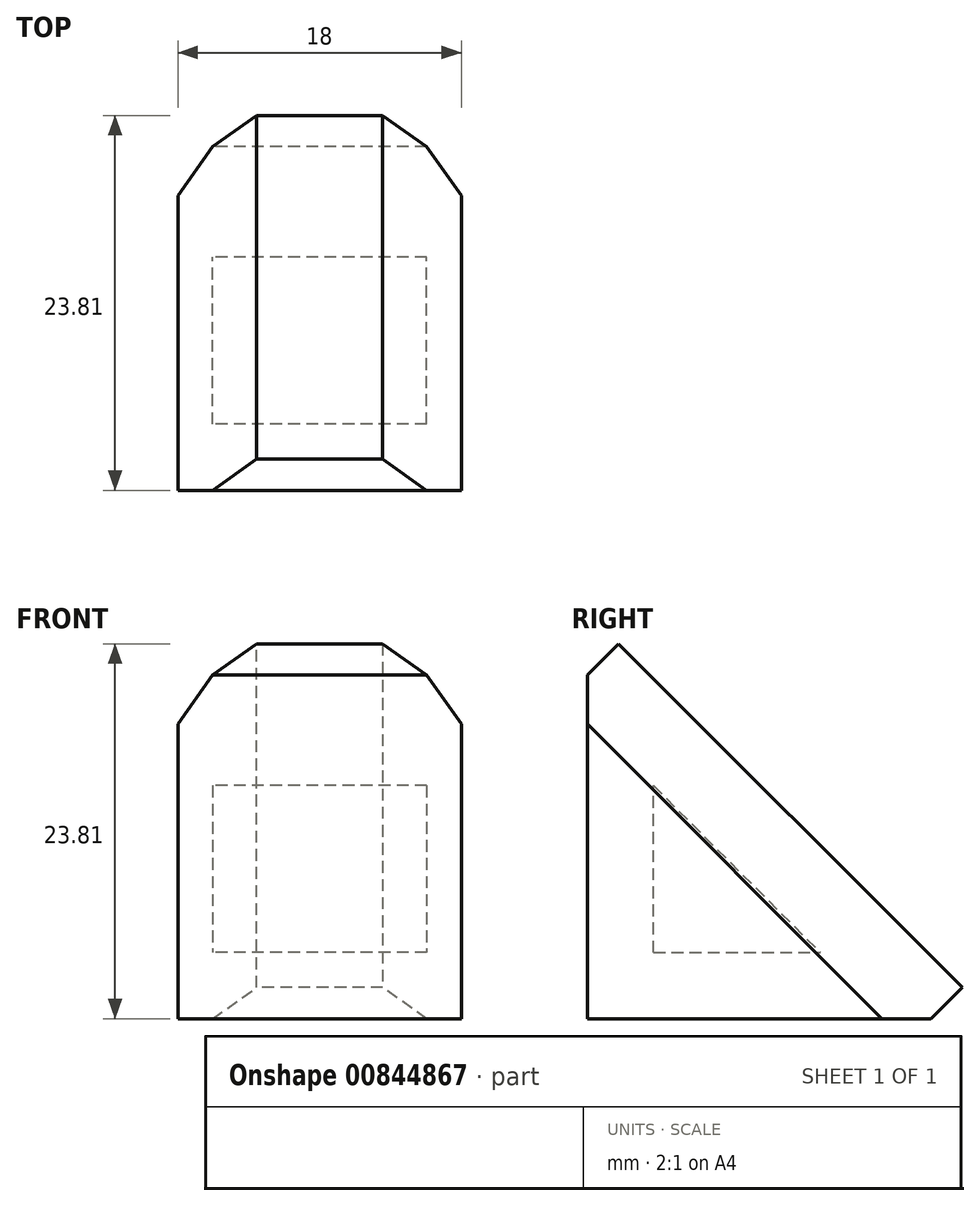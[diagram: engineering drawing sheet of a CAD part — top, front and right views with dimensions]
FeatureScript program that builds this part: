
annotation { "Feature Type Name" : "Feature", "Feature Type Description" : "" }
export const myFeature = defineFeature(function(context is Context, id is Id, definition is map)
    precondition{}
    {
        {
            var Q0;
            Q0=qCreatedBy(makeId("Right.planeOp"),FACE);
            var sketch = newSketch(context, id + "F0", { "sketchPlane" : qUnion([Q0])});
            skLineSegment(sketch, "E0.bottom", {"start": v(0, 0) * mm, "end": v(15, 0) * mm});
            skLineSegment(sketch, "E0.top", {"start": v(0, 15) * mm, "end": v(15, 15) * mm});
            skLineSegment(sketch, "E0.left", {"start": v(0, 0) * mm, "end": v(0, 15) * mm});
            skLineSegment(sketch, "E0.right", {"start": v(15, 0) * mm, "end": v(15, 15) * mm});
            skLineSegment(sketch, "E1", {"start": v(0, 15) * mm, "end": v(15, 0) * mm});
            skLineSegment(sketch, "E2.0", {"start": v(-2, -2) * mm, "end": v(-2, 19.83) * mm});
            skLineSegment(sketch, "E2.1", {"start": v(-2, -2) * mm, "end": v(19.83, -2) * mm});
            skLineSegment(sketch, "E2.2", {"start": v(-2, 19.83) * mm, "end": v(19.83, -2) * mm});
            skSolve(sketch);
        }
        {
            var Q0;
            Q0=makeQuery(id+"F0.imprint","IMPRINT",FACE,{"disambiguationData":[TD([[makeQuery(id+"F0.imprint","IMPRINT",EDGE,{"derivedFrom":sQuery(id+"F0.wireOp",EDGE,"E0.bottom")}),1.0]])]});
            extrude(context, id + "F1", {"entities" : qUnion([Q0]), "depth" : 18 * mm, "offsetDistance" : 25 * mm});
        }
        {
            var Q0;
            Q0=makeQuery(id+"F1.opExtrude","SWEPT_FACE",FACE,{"disambiguationData":[OSD([sQuery(id+"F0.wireOp",EDGE,"E1")])]});
            shell(context, id + "F2", {"entities" : qUnion([Q0]), "thickness" : 2.2 * mm});
        }
        {
            var Q0;
            Q0=makeQuery(id+"F1.opExtrude","SWEPT_FACE",FACE,{"disambiguationData":[OSD([sQuery(id+"F0.wireOp",EDGE,"E1")])]});
            var sketch = newSketch(context, id + "F3", { "sketchPlane" : qUnion([Q0])});
            skLineSegment(sketch, "E3.bottom", {"start": v(15.8, -7.5) * mm, "end": v(2.2, -7.5) * mm});
            skLineSegment(sketch, "E3.top", {"start": v(15.8, 7.5) * mm, "end": v(2.2, 7.5) * mm});
            skLineSegment(sketch, "E3.left", {"start": v(15.8, -7.5) * mm, "end": v(15.8, 7.5) * mm});
            skLineSegment(sketch, "E3.right", {"start": v(2.2, -7.5) * mm, "end": v(2.2, 7.5) * mm});
            skSolve(sketch);
        }
        {
            var Q0;
            {var subQ2=sQuery(id+"F0.wireOp",EDGE,"E0.bottom");Q0=makeQuery(id+"F0.imprint","IMPRINT",FACE,{"disambiguationData":[TD([[makeQuery(id+"F0.imprint","IMPRINT",EDGE,{"derivedFrom":subQ2}),-1.0]])]});}
            var Q1;
            {var subQ0=sQuery(id+"F0.wireOp",EDGE,"E1");Q1=makeQuery(id+"F0.imprint","IMPRINT",FACE,{"disambiguationData":[TD([[makeQuery(id+"F0.imprint","IMPRINT",EDGE,{"derivedFrom":subQ0}),1.0]])]});}
            extrude(context, id + "F4", {"entities" : qUnion([Q0, Q1]), "operationType" : NewBodyOperationType.ADD, "depth" : 18 * mm, "offsetDistance" : 25 * mm});
        }
        {
            var Q0;
            Q0=makeQuery(id+"F3.imprint","IMPRINT",FACE,{"disambiguationData":[TD([[makeQuery(id+"F3.imprint","IMPRINT",EDGE,{"derivedFrom":sQuery(id+"F3.wireOp",EDGE,"E3.bottom")}),-1.0]])]});
            extrude(context, id + "F5", {"entities" : qUnion([Q0]), "operationType" : NewBodyOperationType.REMOVE, "depth" : 8.9 * mm, "offsetDistance" : 25 * mm});
        }
        {
            var Q0;
            Q0=makeQuery(id+"F4.opExtrude","SWEPT_FACE",FACE,{"disambiguationData":[OSD([sQuery(id+"F0.wireOp",EDGE,"E2.2")])]});
            extrude(context, id + "F6", {"entities" : qUnion([Q0]), "operationType" : NewBodyOperationType.ADD, "depth" : 2.8 * mm, "offsetDistance" : 25 * mm});
        }
        {
            var Q0;
            Q0=makeQuery(id+"F6.opExtrude","CAP_EDGE",EDGE,{"disambiguationData":[OSD([sQuery(id+"F0.wireOp",EDGE,"E2.2"),sQuery(id+"F3.wireOp",EDGE,"E3.right")])],"isStart":false});
            var Q1;
            Q1=makeQuery(id+"F6.opExtrude","CAP_EDGE",EDGE,{"disambiguationData":[OSD([sQuery(id+"F0.wireOp",EDGE,"E2.2"),sQuery(id+"F3.wireOp",EDGE,"E3.top")])],"isStart":false});
            var Q2;
            Q2=makeQuery(id+"F6.opExtrude","CAP_EDGE",EDGE,{"disambiguationData":[OSD([sQuery(id+"F0.wireOp",EDGE,"E2.2"),sQuery(id+"F3.wireOp",EDGE,"E3.left")])],"isStart":false});
            var Q3;
            Q3=makeQuery(id+"F6.opExtrude","CAP_EDGE",EDGE,{"disambiguationData":[OSD([sQuery(id+"F0.wireOp",EDGE,"E2.2"),sQuery(id+"F3.wireOp",EDGE,"E3.bottom")])],"isStart":false});
            chamfer(context, id + "F7", {"entities" : qUnion([Q0, Q1, Q2, Q3]), "width" : 5 * mm, "tangentPropagation" : true});
        }
    });
